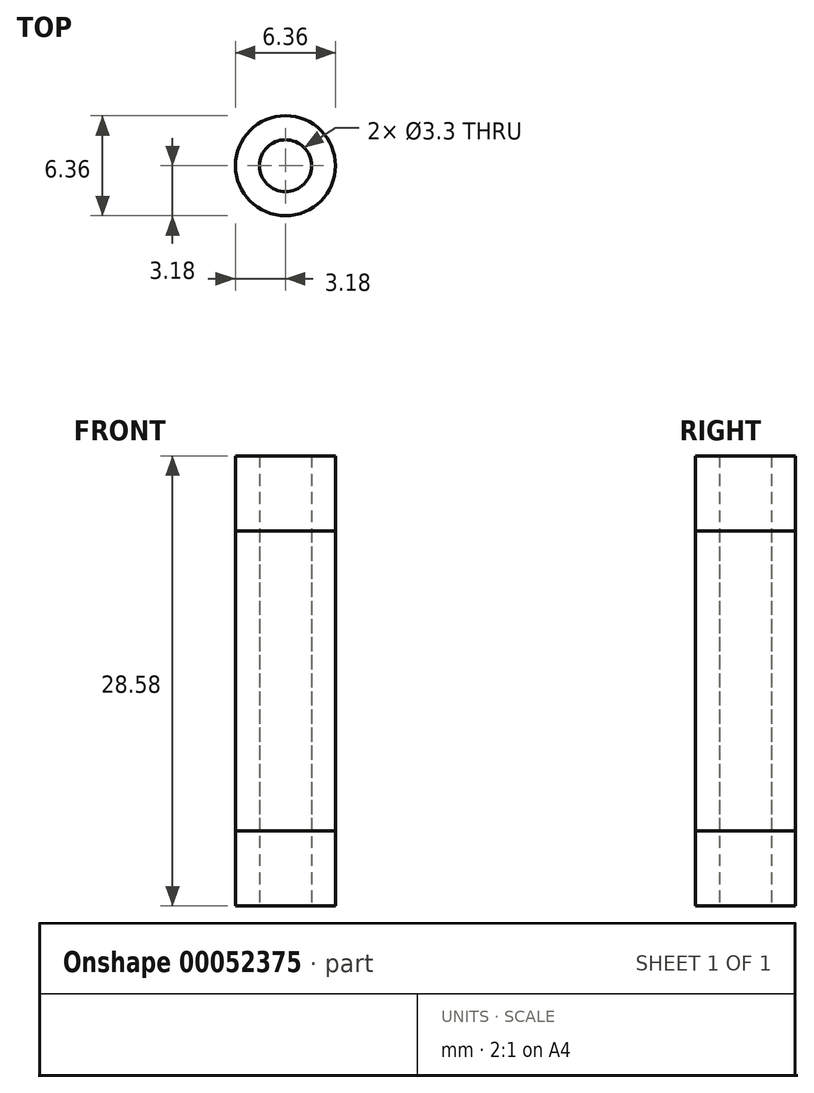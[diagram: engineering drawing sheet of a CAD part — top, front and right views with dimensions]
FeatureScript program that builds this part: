
annotation { "Feature Type Name" : "Feature", "Feature Type Description" : "" }
export const myFeature = defineFeature(function(context is Context, id is Id, definition is map)
    precondition{}
    {
        {
            var Q0;
            Q0=qCreatedBy(makeId("Top.planeOp"),FACE);
            var sketch = newSketch(context, id + "F0", { "sketchPlane" : qUnion([Q0])});
            skCircle(sketch, "E0", {"center": v(0, 0) * mm, "radius": 3.18 * mm});
            skCircle(sketch, "E1", {"center": v(0, 0) * mm, "radius": 1.65 * mm});
            skSolve(sketch);
        }
        {
            var Q0;
            Q0 = qSketchRegion(id + "F0", true);
            extrude(context, id + "F1", {"entities" : qUnion([Q0]), "depth" : 28.57 * mm, "symmetric" : true});
        }
        {
            var Q0;
            Q0=qCreatedBy(makeId("Top.planeOp"),FACE);
            var sketch = newSketch(context, id + "F2", { "sketchPlane" : qUnion([Q0])});
            skCircle(sketch, "E2", {"center": v(0, 0) * mm, "radius": 3.18 * mm});
            skCircle(sketch, "E3", {"center": v(0, 0) * mm, "radius": 1.65 * mm});
            skSolve(sketch);
        }
        {
            var Q0;
            Q0 = qSketchRegion(id + "F2", true);
            extrude(context, id + "F3", {"entities" : qUnion([Q0]), "depth" : 19.05 * mm, "symmetric" : true});
        }
    });
